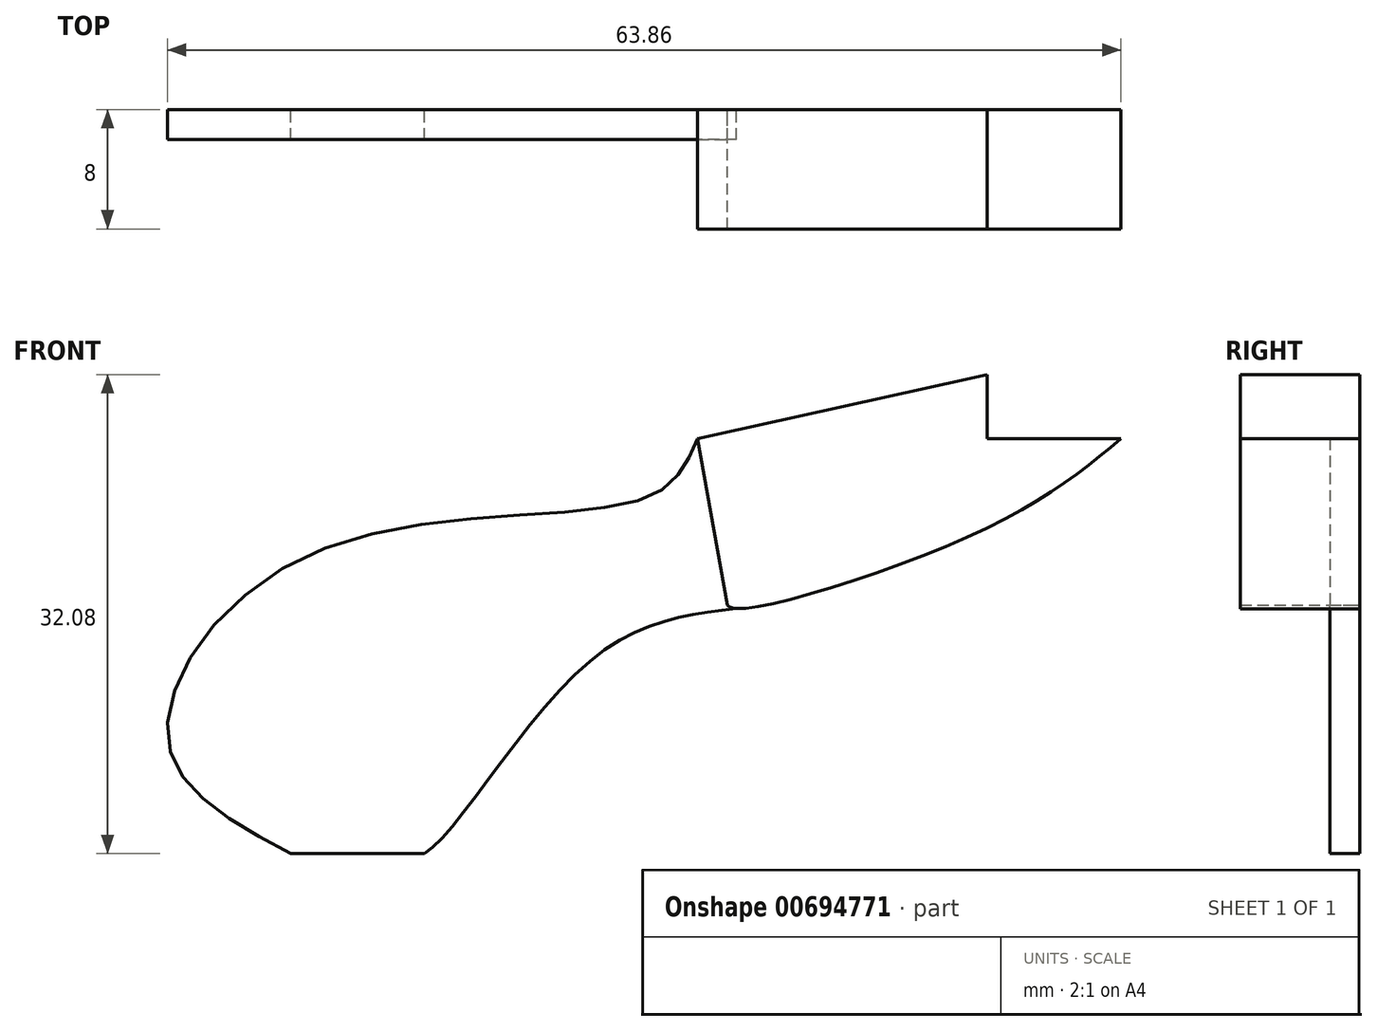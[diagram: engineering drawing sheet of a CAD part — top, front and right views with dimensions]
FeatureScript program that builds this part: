
annotation { "Feature Type Name" : "Feature", "Feature Type Description" : "" }
export const myFeature = defineFeature(function(context is Context, id is Id, definition is map)
    precondition{}
    {
        {
            var Q0;
            Q0=qCreatedBy(makeId("Front.planeOp"),FACE);
            var sketch = newSketch(context, id + "F0", { "sketchPlane" : qUnion([Q0])});
            skFitSpline(sketch, "E0", {"points": [v(20.14, 0) * mm, v(10.82, -6.16) * mm, v(-5.6, -11.38) * mm, v(-6.34, -11) * mm], "startDerivative": vector(-18.27, -15.27) * mm, "endDerivative": vector(-3.9, 4.72) * mm});
            skLineSegment(sketch, "E1", {"start": v(20.14, 0) * mm, "end": v(11.2, 0) * mm});
            skLineSegment(sketch, "E2", {"start": v(11.2, 0) * mm, "end": v(11.2, 4.3) * mm});
            skLineSegment(sketch, "E3", {"start": v(11.2, 4.3) * mm, "end": v(-8.2, 0) * mm});
            skLineSegment(sketch, "E4", {"start": v(-8.2, 0) * mm, "end": v(-6.2, -11.18) * mm});
            skFitSpline(sketch, "E5", {"points": [v(-5.6, -11.38) * mm, v(-15.67, -15.11) * mm, v(-26.49, -27.8) * mm, v(-27.98, -27.8) * mm], "startDerivative": vector(-26.1, -3.02) * mm, "endDerivative": vector(-9.03, 4.04) * mm});
            skFitSpline(sketch, "E6", {"points": [v(-8.2, 0) * mm, v(-11.56, -3.92) * mm, v(-33.95, -7.65) * mm, v(-43.65, -20.33) * mm, v(-35.44, -27.8) * mm], "startDerivative": vector(-12.22, -29.2) * mm, "endDerivative": vector(49.58, -26.53) * mm});
            skLineSegment(sketch, "E7", {"start": v(-35.44, -27.8) * mm, "end": v(-26.49, -27.8) * mm});
            skSolve(sketch);
        }
        {
            var Q0;
            {var subQ0=sQuery(id+"F0.wireOp",EDGE,"E1");Q0=makeQuery(id+"F0.imprint","IMPRINT",FACE,{"disambiguationData":[TD([[makeQuery(id+"F0.imprint","IMPRINT",EDGE,{"derivedFrom":subQ0}),1.0]])]});}
            var Q1;
            {var subQ0=sQuery(id+"F0.wireOp",EDGE,"E7");var subQ1=sQuery(id+"F0.wireOp",EDGE,"E5");var subQ2=makeQuery(id+"F0.imprint","INTERSECT",VERTEX,{"disambiguationData":[OD(0.0)],"derivedFrom":[subQ1,subQ0]});Q1=makeQuery(id+"F0.imprint","IMPRINT",FACE,{"disambiguationData":[TD([[makeQuery(id+"F0.imprint","IMPRINT",EDGE,{"disambiguationData":[TD([[subQ2,-1.0]])],"derivedFrom":subQ1}),-1.0]])]});}
            extrude(context, id + "F1", {"entities" : qUnion([Q0, Q1]), "depth" : 8 * mm, "offsetDistance" : 25 * mm});
        }
        {
            var Q0;
            {var subQ0=sQuery(id+"F0.wireOp",EDGE,"E6");Q0=makeQuery(id+"F0.imprint","IMPRINT",FACE,{"disambiguationData":[TD([[makeQuery(id+"F0.imprint","IMPRINT",EDGE,{"derivedFrom":subQ0}),1.0]])]});}
            extrude(context, id + "F2", {"entities" : qUnion([Q0]), "depth" : 2 * mm, "offsetDistance" : 25 * mm});
        }
    });
